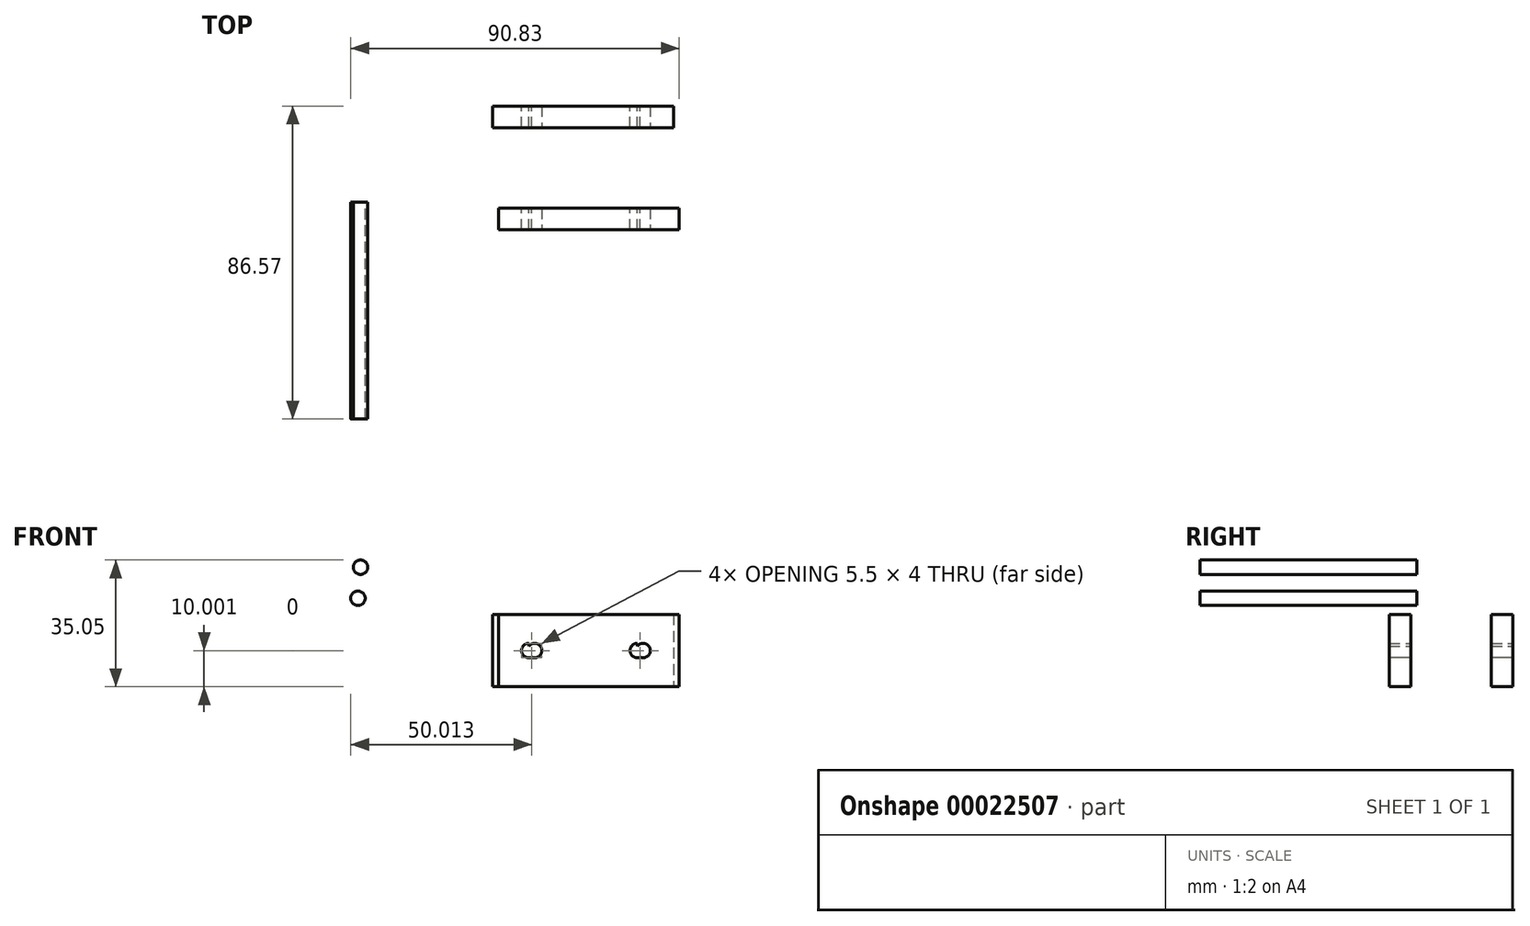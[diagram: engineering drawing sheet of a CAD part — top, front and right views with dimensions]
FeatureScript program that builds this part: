
annotation { "Feature Type Name" : "Feature", "Feature Type Description" : "" }
export const myFeature = defineFeature(function(context is Context, id is Id, definition is map)
    precondition{}
    {
        {
            var Q0;
            Q0=qCreatedBy(makeId("Top.planeOp"),FACE);
            var sketch = newSketch(context, id + "F0", { "sketchPlane" : qUnion([Q0])});
            skLineSegment(sketch, "E0.bottom", {"start": v(-17.23, 26.57) * mm, "end": v(32.77, 26.57) * mm});
            skLineSegment(sketch, "E0.top", {"start": v(-17.23, 20.57) * mm, "end": v(32.77, 20.57) * mm});
            skLineSegment(sketch, "E0.left", {"start": v(-17.23, 26.57) * mm, "end": v(-17.23, 20.57) * mm});
            skLineSegment(sketch, "E0.right", {"start": v(32.77, 26.57) * mm, "end": v(32.77, 20.57) * mm});
            skSolve(sketch);
        }
        {
            var Q0;
            Q0=qCreatedBy(makeId("Top.planeOp"),FACE);
            var sketch = newSketch(context, id + "F1", { "sketchPlane" : qUnion([Q0])});
            skLineSegment(sketch, "E1.bottom", {"start": v(-15.62, -1.68) * mm, "end": v(34.38, -1.68) * mm});
            skLineSegment(sketch, "E1.top", {"start": v(-15.62, -7.68) * mm, "end": v(34.38, -7.68) * mm});
            skLineSegment(sketch, "E1.left", {"start": v(-15.62, -1.68) * mm, "end": v(-15.62, -7.68) * mm});
            skLineSegment(sketch, "E1.right", {"start": v(34.38, -1.68) * mm, "end": v(34.38, -7.68) * mm});
            skSolve(sketch);
        }
        {
            var Q0;
            Q0=makeQuery(id+"F0.imprint","IMPRINT",FACE,{"disambiguationData":[TD([[makeQuery(id+"F0.imprint","IMPRINT",EDGE,{"derivedFrom":sQuery(id+"F0.wireOp",EDGE,"E0.bottom")}),-1.0]])]});
            extrude(context, id + "F2", {"entities" : qUnion([Q0]), "depth" : 20 * mm});
        }
        {
            var Q0;
            Q0=makeQuery(id+"F1.imprint","IMPRINT",FACE,{"disambiguationData":[TD([[makeQuery(id+"F1.imprint","IMPRINT",EDGE,{"derivedFrom":sQuery(id+"F1.wireOp",EDGE,"E1.bottom")}),-1.0]])]});
            extrude(context, id + "F3", {"entities" : qUnion([Q0]), "depth" : 20 * mm});
        }
        {
            var Q0;
            Q0=makeQuery(id+"F3.opExtrude","SWEPT_FACE",FACE,{"disambiguationData":[OSD([sQuery(id+"F1.wireOp",EDGE,"E1.top")])]});
            var sketch = newSketch(context, id + "F4", { "sketchPlane" : qUnion([Q0])});
            skCircle(sketch, "E2", {"center": v(-5.62, 10) * mm, "radius": 2 * mm});
            skCircle(sketch, "E3", {"center": v(24.38, 10) * mm, "radius": 2 * mm});
            skLineSegment(sketch, "E4", {"start": v(-5.62, 20) * mm, "end": v(-5.62, 0) * mm});
            skLineSegment(sketch, "E5", {"start": v(24.38, 20) * mm, "end": v(24.38, 0) * mm});
            skSolve(sketch);
        }
        {
            var Q0;
            {var subQ0=sQuery(id+"F4.wireOp",EDGE,"E4");var subQ1=sQuery(id+"F4.wireOp",EDGE,"E2");var subQ3=makeQuery(id+"F4.imprint","INTERSECT",VERTEX,{"disambiguationData":[OD(0.0)],"derivedFrom":[subQ1,subQ0]});Q0=makeQuery(id+"F4.imprint","IMPRINT",FACE,{"disambiguationData":[TD([[makeQuery(id+"F4.imprint","IMPRINT",EDGE,{"disambiguationData":[TD([[subQ3,-1.0]])],"derivedFrom":subQ1}),1.0]])]});}
            var Q1;
            {var subQ0=sQuery(id+"F4.wireOp",EDGE,"E4");var subQ1=sQuery(id+"F4.wireOp",EDGE,"E2");var subQ3=makeQuery(id+"F4.imprint","INTERSECT",VERTEX,{"disambiguationData":[OD(0.0)],"derivedFrom":[subQ1,subQ0]});Q1=makeQuery(id+"F4.imprint","IMPRINT",FACE,{"disambiguationData":[TD([[makeQuery(id+"F4.imprint","IMPRINT",EDGE,{"disambiguationData":[TD([[subQ3,1.0]])],"derivedFrom":subQ1}),1.0]])]});}
            var Q2;
            {var subQ0=sQuery(id+"F4.wireOp",EDGE,"E5");var subQ1=sQuery(id+"F4.wireOp",EDGE,"E3");var subQ3=makeQuery(id+"F4.imprint","INTERSECT",VERTEX,{"disambiguationData":[OD(0.0)],"derivedFrom":[subQ1,subQ0]});Q2=makeQuery(id+"F4.imprint","IMPRINT",FACE,{"disambiguationData":[TD([[makeQuery(id+"F4.imprint","IMPRINT",EDGE,{"disambiguationData":[TD([[subQ3,-1.0]])],"derivedFrom":subQ1}),1.0]])]});}
            var Q3;
            {var subQ0=sQuery(id+"F4.wireOp",EDGE,"E5");var subQ1=sQuery(id+"F4.wireOp",EDGE,"E3");var subQ3=makeQuery(id+"F4.imprint","INTERSECT",VERTEX,{"disambiguationData":[OD(0.0)],"derivedFrom":[subQ1,subQ0]});Q3=makeQuery(id+"F4.imprint","IMPRINT",FACE,{"disambiguationData":[TD([[makeQuery(id+"F4.imprint","IMPRINT",EDGE,{"disambiguationData":[TD([[subQ3,1.0]])],"derivedFrom":subQ1}),1.0]])]});}
            extrude(context, id + "F5", {"entities" : qUnion([Q0, Q1, Q2, Q3]), "operationType" : NewBodyOperationType.REMOVE, "endBound" : BoundingType.THROUGH_ALL, "oppositeDirection" : true, "depth" : 25 * mm});
        }
        {
            var Q0;
            Q0=makeQuery(id+"F2.opExtrude","SWEPT_FACE",FACE,{"disambiguationData":[OSD([sQuery(id+"F0.wireOp",EDGE,"E0.bottom")])]});
            var sketch = newSketch(context, id + "F6", { "sketchPlane" : qUnion([Q0])});
            skCircle(sketch, "E6", {"center": v(-22.77, 10) * mm, "radius": 2 * mm});
            skCircle(sketch, "E7", {"center": v(7.23, 10) * mm, "radius": 2 * mm});
            skLineSegment(sketch, "E8", {"start": v(-22.77, 20) * mm, "end": v(-22.77, 0) * mm});
            skLineSegment(sketch, "E9", {"start": v(7.23, 20) * mm, "end": v(7.23, 0) * mm});
            skSolve(sketch);
        }
        {
            var Q0;
            {var subQ0=sQuery(id+"F6.wireOp",EDGE,"E8");var subQ1=sQuery(id+"F6.wireOp",EDGE,"E6");var subQ3=makeQuery(id+"F6.imprint","INTERSECT",VERTEX,{"disambiguationData":[OD(0.0)],"derivedFrom":[subQ1,subQ0]});Q0=makeQuery(id+"F6.imprint","IMPRINT",FACE,{"disambiguationData":[TD([[makeQuery(id+"F6.imprint","IMPRINT",EDGE,{"disambiguationData":[TD([[subQ3,-1.0]])],"derivedFrom":subQ1}),1.0]])]});}
            var Q1;
            {var subQ0=sQuery(id+"F6.wireOp",EDGE,"E8");var subQ1=sQuery(id+"F6.wireOp",EDGE,"E6");var subQ3=makeQuery(id+"F6.imprint","INTERSECT",VERTEX,{"disambiguationData":[OD(0.0)],"derivedFrom":[subQ1,subQ0]});Q1=makeQuery(id+"F6.imprint","IMPRINT",FACE,{"disambiguationData":[TD([[makeQuery(id+"F6.imprint","IMPRINT",EDGE,{"disambiguationData":[TD([[subQ3,1.0]])],"derivedFrom":subQ1}),1.0]])]});}
            var Q2;
            {var subQ0=sQuery(id+"F6.wireOp",EDGE,"E9");var subQ1=sQuery(id+"F6.wireOp",EDGE,"E7");var subQ3=makeQuery(id+"F6.imprint","INTERSECT",VERTEX,{"disambiguationData":[OD(0.0)],"derivedFrom":[subQ1,subQ0]});Q2=makeQuery(id+"F6.imprint","IMPRINT",FACE,{"disambiguationData":[TD([[makeQuery(id+"F6.imprint","IMPRINT",EDGE,{"disambiguationData":[TD([[subQ3,-1.0]])],"derivedFrom":subQ1}),1.0]])]});}
            var Q3;
            {var subQ0=sQuery(id+"F6.wireOp",EDGE,"E9");var subQ1=sQuery(id+"F6.wireOp",EDGE,"E7");var subQ3=makeQuery(id+"F6.imprint","INTERSECT",VERTEX,{"disambiguationData":[OD(0.0)],"derivedFrom":[subQ1,subQ0]});Q3=makeQuery(id+"F6.imprint","IMPRINT",FACE,{"disambiguationData":[TD([[makeQuery(id+"F6.imprint","IMPRINT",EDGE,{"disambiguationData":[TD([[subQ3,1.0]])],"derivedFrom":subQ1}),1.0]])]});}
            extrude(context, id + "F7", {"entities" : qUnion([Q0, Q1, Q2, Q3]), "operationType" : NewBodyOperationType.REMOVE, "endBound" : BoundingType.THROUGH_ALL, "oppositeDirection" : true, "depth" : 25 * mm});
        }
        {
            var Q0;
            Q0=qCreatedBy(makeId("Front.planeOp"),FACE);
            var sketch = newSketch(context, id + "F8", { "sketchPlane" : qUnion([Q0])});
            skCircle(sketch, "E10", {"center": v(-53.74, 33.05) * mm, "radius": 2 * mm});
            skCircle(sketch, "E11", {"center": v(-54.45, 24.47) * mm, "radius": 2 * mm});
            skSolve(sketch);
        }
        {
            var Q0;
            Q0=makeQuery(id+"F8.imprint","IMPRINT",FACE,{"disambiguationData":[TD([[makeQuery(id+"F8.imprint","IMPRINT",EDGE,{"derivedFrom":sQuery(id+"F8.wireOp",EDGE,"E11")}),1.0]])]});
            extrude(context, id + "F9", {"entities" : qUnion([Q0]), "depth" : 60 * mm});
        }
        {
            var Q0;
            Q0=makeQuery(id+"F8.imprint","IMPRINT",FACE,{"disambiguationData":[TD([[makeQuery(id+"F8.imprint","IMPRINT",EDGE,{"derivedFrom":sQuery(id+"F8.wireOp",EDGE,"E10")}),1.0]])]});
            extrude(context, id + "F10", {"entities" : qUnion([Q0]), "depth" : 60 * mm});
        }
    });
